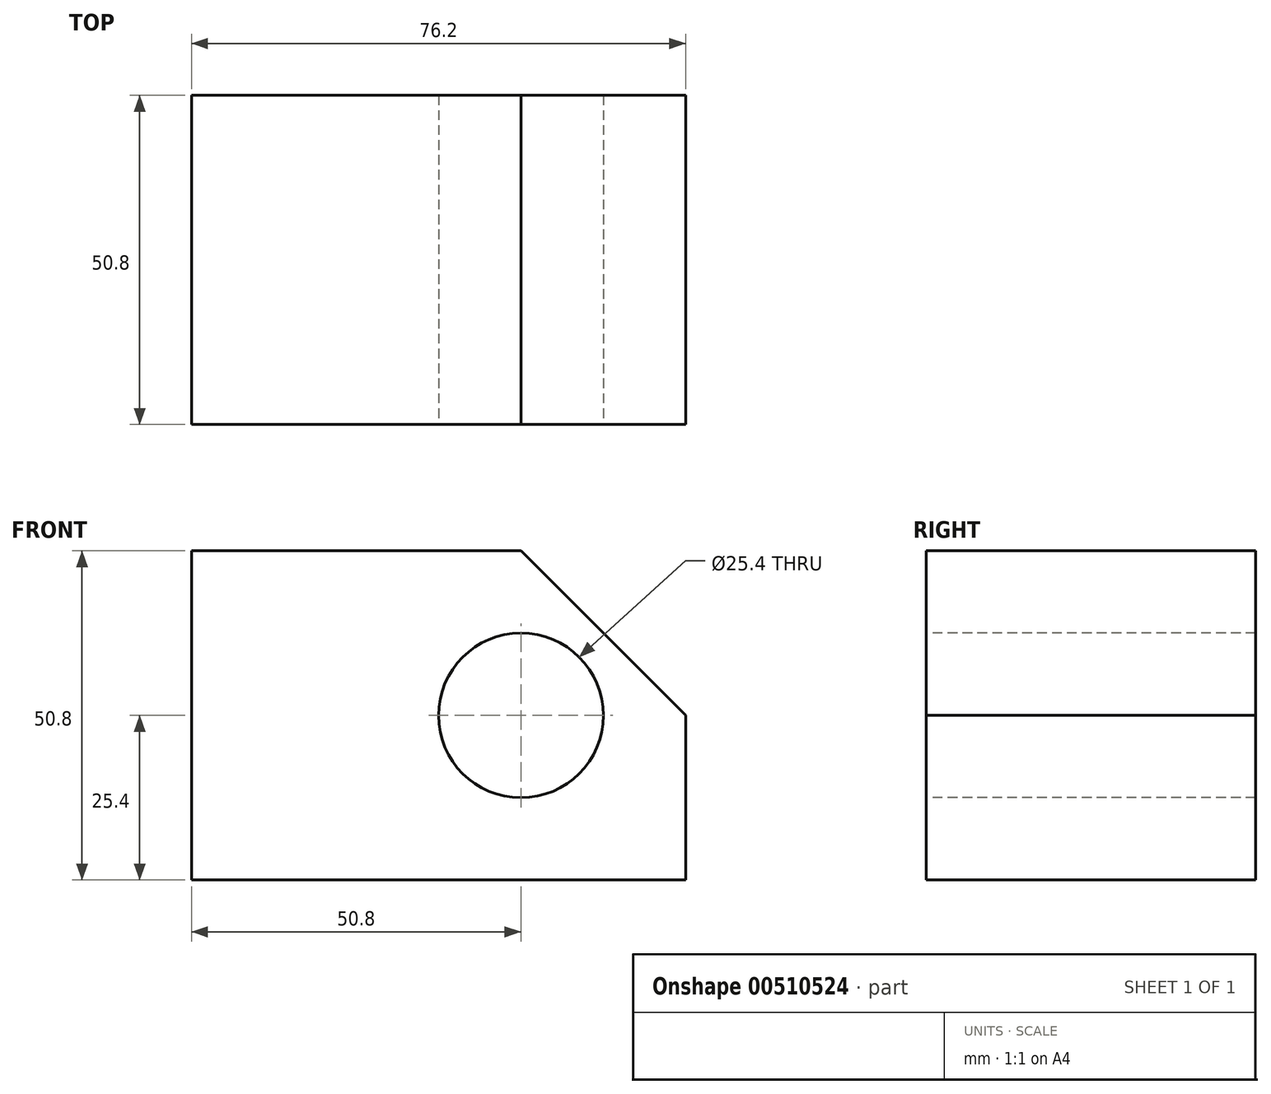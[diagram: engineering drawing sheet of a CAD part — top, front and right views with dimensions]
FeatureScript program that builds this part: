
annotation { "Feature Type Name" : "Feature", "Feature Type Description" : "" }
export const myFeature = defineFeature(function(context is Context, id is Id, definition is map)
    precondition{}
    {
        {
            var Q0;
            Q0=qCreatedBy(makeId("Front.planeOp"),FACE);
            var sketch = newSketch(context, id + "F0", { "sketchPlane" : qUnion([Q0])});
            skLineSegment(sketch, "E0.bottom", {"start": v(0, 0) * mm, "end": v(-76.2, 0) * mm});
            skLineSegment(sketch, "E0.top", {"start": v(0, 50.8) * mm, "end": v(-76.2, 50.8) * mm});
            skLineSegment(sketch, "E0.left", {"start": v(0, 0) * mm, "end": v(0, 50.8) * mm});
            skLineSegment(sketch, "E0.right", {"start": v(-76.2, 0) * mm, "end": v(-76.2, 50.8) * mm});
            skSolve(sketch);
        }
        {
            var Q0;
            Q0 = qSketchRegion(id + "F0", true);
            extrude(context, id + "F1", {"entities" : qUnion([Q0]), "depth" : 50.8 * mm});
        }
        {
            var Q0;
            Q0=makeQuery(id+"F1.opExtrude","SWEPT_EDGE",EDGE,{"disambiguationData":[OSD([sQuery(id+"F0.wireOp",EDGE,"E0.top"),sQuery(id+"F0.wireOp",EDGE,"E0.left")])]});
            chamfer(context, id + "F2", {"entities" : qUnion([Q0]), "width" : 25.4 * mm, "tangentPropagation" : true});
        }
        {
            var Q0;
            Q0=makeQuery(id+"F1.opExtrude","CAP_FACE",FACE,{"disambiguationData":[OSD([sQuery(id+"F0.wireOp",EDGE,"E0.bottom"),sQuery(id+"F0.wireOp",EDGE,"E0.top"),sQuery(id+"F0.wireOp",EDGE,"E0.left"),sQuery(id+"F0.wireOp",EDGE,"E0.right")])],"isStart":false});
            var sketch = newSketch(context, id + "F3", { "sketchPlane" : qUnion([Q0])});
            skCircle(sketch, "E1", {"center": v(-25.4, 25.4) * mm, "radius": 12.7 * mm});
            skSolve(sketch);
        }
        {
            var Q0;
            Q0 = qSketchRegion(id + "F3", true);
            extrude(context, id + "F4", {"entities" : qUnion([Q0]), "operationType" : NewBodyOperationType.REMOVE, "oppositeDirection" : true, "depth" : 50.8 * mm});
        }
    });
